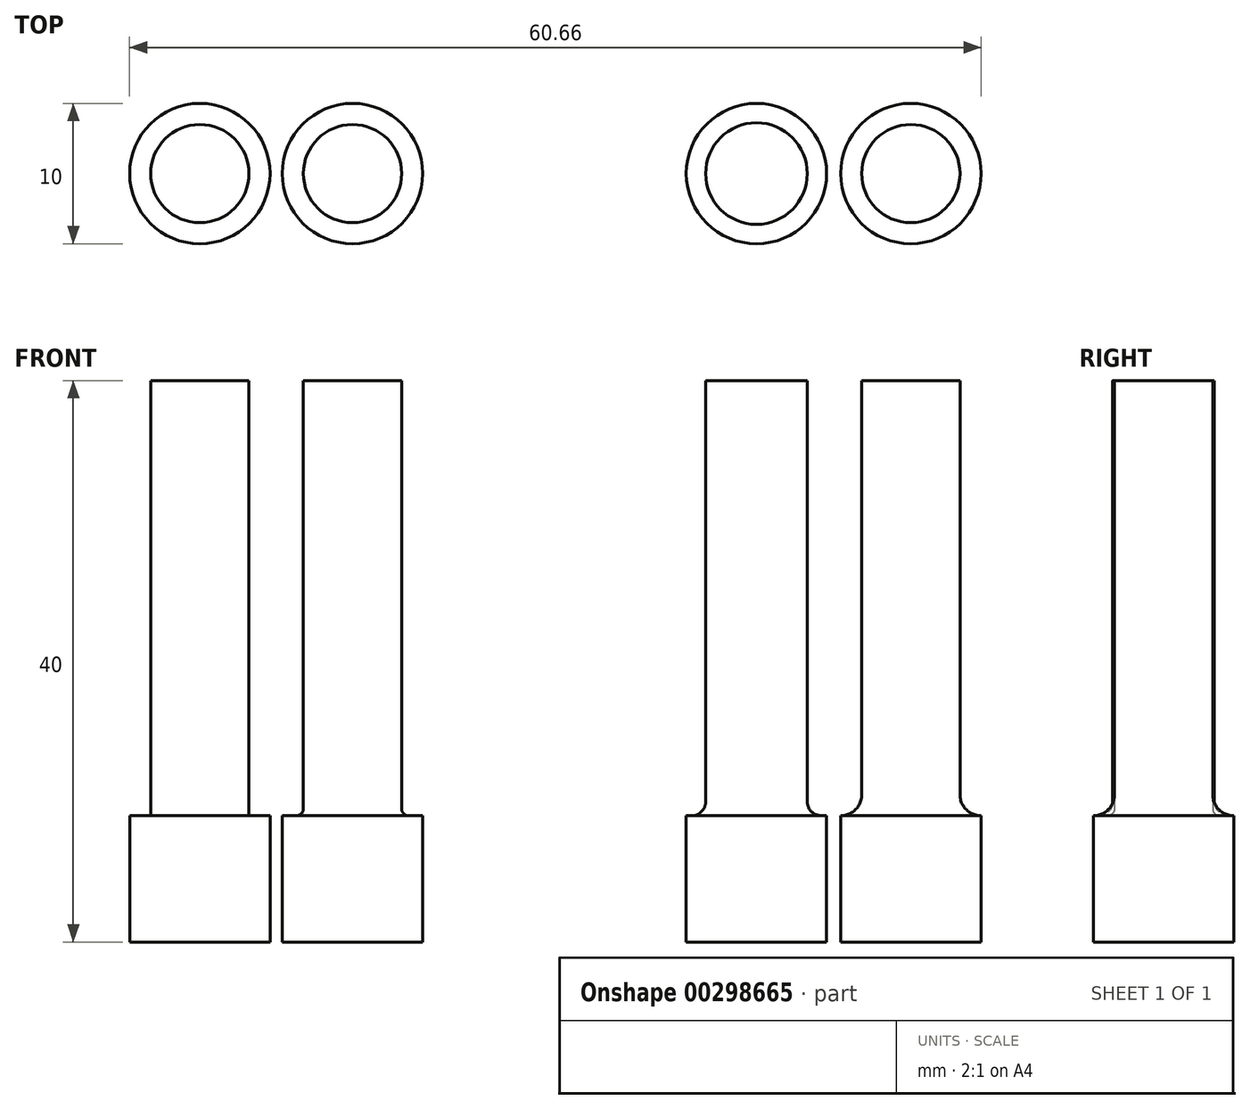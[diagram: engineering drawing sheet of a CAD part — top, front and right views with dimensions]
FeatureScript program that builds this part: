
annotation { "Feature Type Name" : "Feature", "Feature Type Description" : "" }
export const myFeature = defineFeature(function(context is Context, id is Id, definition is map)
    precondition{}
    {
        {
            var Q0;
            Q0=qCreatedBy(makeId("Top.planeOp"),FACE);
            var sketch = newSketch(context, id + "F0", { "sketchPlane" : qUnion([Q0])});
            skCircle(sketch, "E0", {"center": v(-9.46, -10.49) * mm, "radius": 3.5 * mm});
            skLineSegment(sketch, "E1", {"start": v(-9.46, -10.49) * mm, "end": v(16.85, -10.49) * mm, "construction": true});
            skCircle(sketch, "E2", {"center": v(1.42, -10.49) * mm, "radius": 3.5 * mm});
            skCircle(sketch, "E3", {"center": v(30.2, -10.49) * mm, "radius": 3.62 * mm});
            skCircle(sketch, "E4", {"center": v(41.2, -10.49) * mm, "radius": 3.5 * mm});
            skSolve(sketch);
        }
        {
            var Q0;
            Q0 = qSketchRegion(id + "F0", true);
            extrude(context, id + "F1", {"entities" : qUnion([Q0]), "depth" : 40 * mm});
        }
        {
            var Q0;
            Q0=qCreatedBy(makeId("Top.planeOp"),FACE);
            var sketch = newSketch(context, id + "F2", { "sketchPlane" : qUnion([Q0])});
            skCircle(sketch, "E5", {"center": v(-9.46, -10.49) * mm, "radius": 5 * mm});
            skCircle(sketch, "E6", {"center": v(1.42, -10.49) * mm, "radius": 5 * mm});
            skCircle(sketch, "E7", {"center": v(30.2, -10.49) * mm, "radius": 5 * mm});
            skCircle(sketch, "E8", {"center": v(41.2, -10.49) * mm, "radius": 5 * mm});
            skSolve(sketch);
        }
        {
            var Q0;
            Q0 = qSketchRegion(id + "F2", true);
            extrude(context, id + "F3", {"entities" : qUnion([Q0]), "operationType" : NewBodyOperationType.ADD, "depth" : 9 * mm});
        }
        {
            var Q0;
            Q0=makeQuery(id+"F3.boolean.opBoolean","INTERSECT",EDGE,{"derivedFrom":[makeQuery(id+"F1.opExtrude","SWEPT_FACE",FACE,{"disambiguationData":[OSD([sQuery(id+"F0.wireOp",EDGE,"E2")])]}),makeQuery(id+"F3.opExtrude","CAP_FACE",FACE,{"disambiguationData":[OSD([sQuery(id+"F2.wireOp",EDGE,"E6")])],"isStart":false})]});
            fillet(context, id + "F4", {"entities" : qUnion([Q0]), "radius" : 0.5 * mm, "tangentPropagation" : true, "allowEdgeOverflow" : false});
        }
        {
            var Q0;
            Q0=makeQuery(id+"F3.boolean.opBoolean","INTERSECT",EDGE,{"derivedFrom":[makeQuery(id+"F1.opExtrude","SWEPT_FACE",FACE,{"disambiguationData":[OSD([sQuery(id+"F0.wireOp",EDGE,"E3")])]}),makeQuery(id+"F3.opExtrude","CAP_FACE",FACE,{"disambiguationData":[OSD([sQuery(id+"F2.wireOp",EDGE,"E7")])],"isStart":false})]});
            fillet(context, id + "F5", {"entities" : qUnion([Q0]), "radius" : 1 * mm, "tangentPropagation" : true, "allowEdgeOverflow" : false});
        }
        {
            var Q0;
            Q0=makeQuery(id+"F3.boolean.opBoolean","INTERSECT",EDGE,{"derivedFrom":[makeQuery(id+"F1.opExtrude","SWEPT_FACE",FACE,{"disambiguationData":[OSD([sQuery(id+"F0.wireOp",EDGE,"E4")])]}),makeQuery(id+"F3.opExtrude","CAP_FACE",FACE,{"disambiguationData":[OSD([sQuery(id+"F2.wireOp",EDGE,"E8")])],"isStart":false})]});
            fillet(context, id + "F6", {"entities" : qUnion([Q0]), "radius" : 1.5 * mm, "tangentPropagation" : true, "allowEdgeOverflow" : false});
        }
    });
